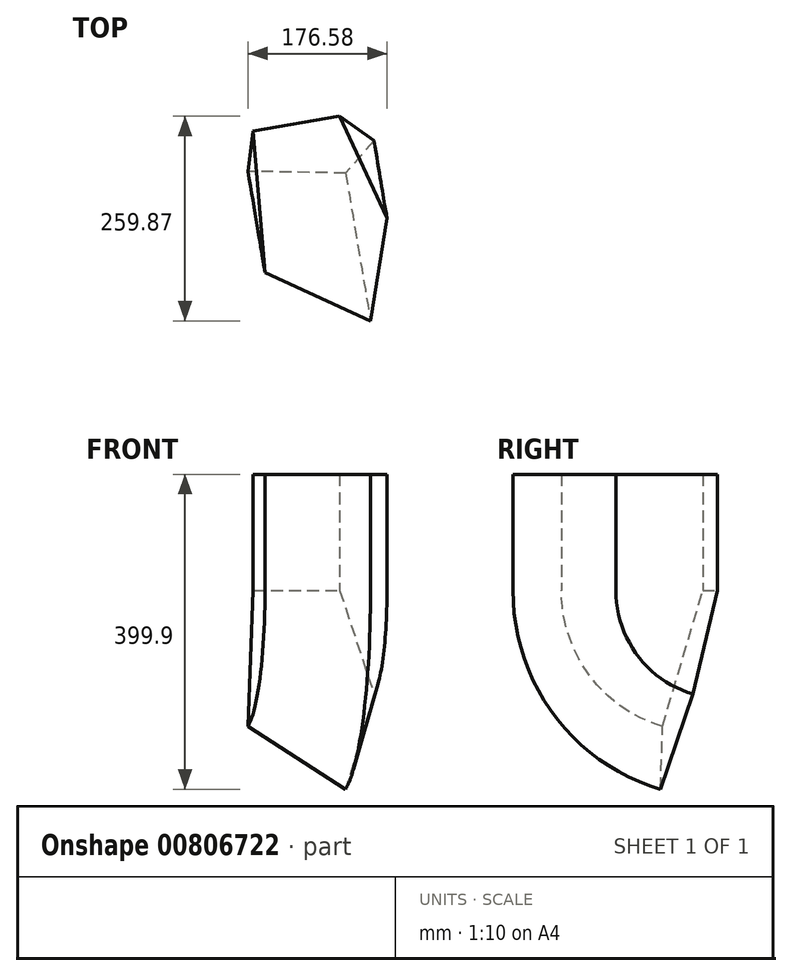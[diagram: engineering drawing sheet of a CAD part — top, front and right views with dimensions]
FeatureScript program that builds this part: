
annotation { "Feature Type Name" : "Feature", "Feature Type Description" : "" }
export const myFeature = defineFeature(function(context is Context, id is Id, definition is map)
    precondition{}
    {
        {
            var Q0;
            Q0=qCreatedBy(makeId("Top.planeOp"),FACE);
            var sketch = newSketch(context, id + "F0", { "sketchPlane" : qUnion([Q0])});
            skLineSegment(sketch, "E0", {"start": v(170.3, -8.6) * mm, "end": v(149.48, -139.53) * mm});
            skLineSegment(sketch, "E1", {"start": v(149.48, -139.53) * mm, "end": v(15.36, -77.9) * mm});
            skLineSegment(sketch, "E2", {"start": v(15.36, -77.9) * mm, "end": v(0, 101.75) * mm});
            skLineSegment(sketch, "E3", {"start": v(0, 101.75) * mm, "end": v(110.34, 120.34) * mm});
            skLineSegment(sketch, "E4", {"start": v(110.34, 120.34) * mm, "end": v(170.3, -8.6) * mm});
            skSolve(sketch);
        }
        {
            var Q0;
            Q0=makeQuery(id+"F0.imprint","IMPRINT",FACE,{"disambiguationData":[TD([[makeQuery(id+"F0.imprint","IMPRINT",EDGE,{"derivedFrom":sQuery(id+"F0.wireOp",EDGE,"E0")}),-1.0]])]});
            var Q1;
            Q1=sQuery(id+"F0.wireOp",EDGE,"E3");
            revolve(context, id + "F1", {"surfaceOperationType" : NewSurfaceOperationType.NEW, "entities" : qUnion([Q0]), "axis" : qUnion([Q1]), "revolveType" : RevolveType.ONE_DIRECTION, "angle" : 74 * degree});
        }
        {
            var Q0;
            Q0 = qSketchRegion(id + "F0", true);
            extrude(context, id + "F2", {"entities" : qUnion([Q0]), "operationType" : NewBodyOperationType.ADD, "depth" : 147.32 * mm, "offsetDistance" : 25.4 * mm});
        }
    });
